# Revit family: ARCTIC.OPL ECO LED
name_source: partatom
category: Осветительные приборы
revit_build: Autodesk Revit 2016 (Build: 20150220_1215(x64)
units: mm (PartAtom-declared; Revit-internal decimal feet)

## family parameters
Источник света = Да
Общий = Нет
Основа = Грань
При загрузке вырезать с полостями = Нет
Размер круглого соединителя = Использовать диаметр
Тип детали = Нормальный
Точка расчета площади = Нет

## types (1)
- ARCTIC.OPL ECO LED
    ADSK_Единица измерения = Шт.
    ADSK_Завод-изготовитель = ООО МГК Световые технологии
    ADSK_Код изделия = 1088000100
    ADSK_Количество фаз = 1
    ADSK_Количество фаз числовое = 1
    ADSK_Коэффициент мощности = 0.96
    ADSK_Масса = 4.3
    ADSK_Наименование = Промышленный светильник с высокой степенью защиты IP65 и высокой светоотдачей. Большое количество модификаций, различающихся габаритными размерами и световым потоком, для замены светильников типа ЛСП
    ADSK_Напряжение = 230 В
    ADSK_Номинальная мощность = 0 кВт
    ADSK_Полная мощность = 0 кВ·А
    ADSK_Размер_Высота = 110 мм
    ADSK_Размер_Длина = 1276 мм
    ADSK_Размер_Ширина = 170 мм
    ADSK_Ток = 0 А
    ADSK_Энергоэффективность = 111 лм/Вт
    IP Class = IP65
    URL = https://ltcompany.com
    Блок аварийного питания = Нет
    Видимая форма излучения при визуализации = Нет
    Группа модели = Светильники
    Изготовитель = ООО МГК Световые технологии
    Излучение по длине прямоугольника = 1276 мм
    Излучение по ширине прямоугольника = 170 мм
    Класс Защиты = II
    Класс пожароопасности = П-II,IIа
    Климатическая зона = УХЛ2
    Код по классификатору = D5020200
    Корпус = Корпус белый пластик
    Крепление = 5 мм
    Крепления.ширина = 930 мм
    Область использования = Магазины/бутики, Промышленные предприятия, Складские объекты
    Описание = Промышленный светильник с высокой степенью защиты IP65 и высокой светоотдачей. Большое количество модификаций, различающихся габаритными размерами и световым потоком, для замены светильников типа ЛСП
    Отметка по умолчанию = 0 мм
    Плафон = Плафон самосвечение
    Полная установленная мощность = 0 кВ·А
    Разработчик = ООО ПРОРУБИМ
    Разработчик (телефон) = +7 (495) 649-85-43
    Светофильтр = 16777215
    Смещение цветовой температуры при затухании лампы = <Нет>
    Тип ИС = LED
    Тип ПРА = Драйвер
    Тип продукции = Светильник
    Угол наклона = -90.00°
    Файл фотометрической сетки = generic
